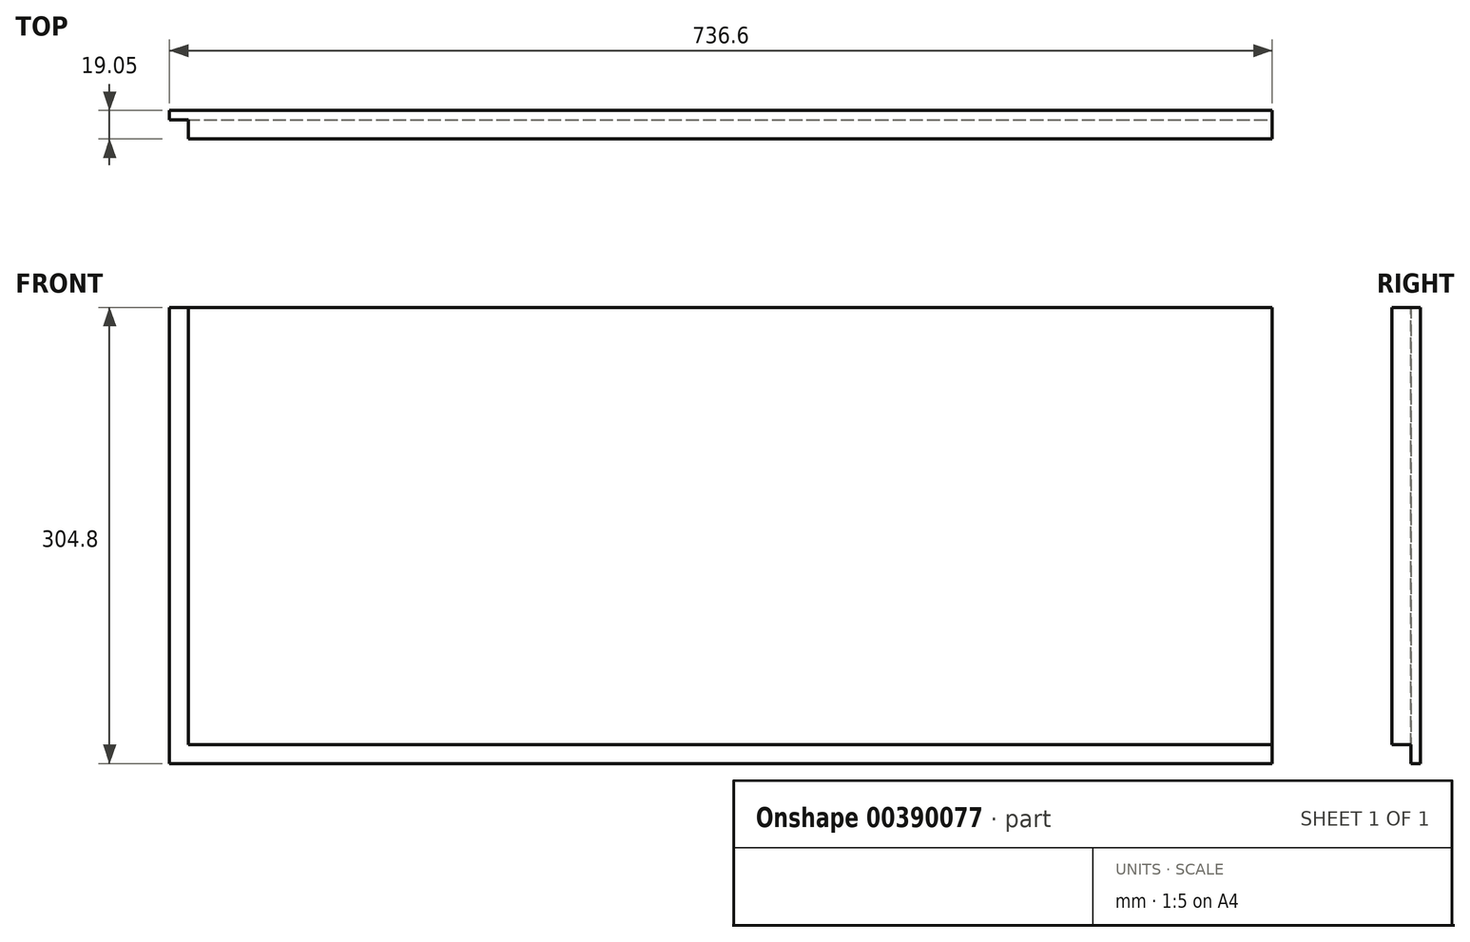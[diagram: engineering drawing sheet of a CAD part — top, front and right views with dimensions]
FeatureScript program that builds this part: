
annotation { "Feature Type Name" : "Feature", "Feature Type Description" : "" }
export const myFeature = defineFeature(function(context is Context, id is Id, definition is map)
    precondition{}
    {
        {
            var Q0;
            Q0=qCreatedBy(makeId("Front.planeOp"),FACE);
            var sketch = newSketch(context, id + "F0", { "sketchPlane" : qUnion([Q0])});
            skLineSegment(sketch, "E0.bottom", {"start": v(0, 0) * mm, "end": v(736.6, 0) * mm});
            skLineSegment(sketch, "E0.top", {"start": v(0, 304.8) * mm, "end": v(736.6, 304.8) * mm});
            skLineSegment(sketch, "E0.left", {"start": v(0, 0) * mm, "end": v(0, 304.8) * mm});
            skLineSegment(sketch, "E0.right", {"start": v(736.6, 0) * mm, "end": v(736.6, 304.8) * mm});
            skSolve(sketch);
        }
        {
            var Q0;
            Q0 = qSketchRegion(id + "F0", true);
            var Q1;
            Q1=makeQuery(id+"F0.imprint","IMPRINT",FACE,{"disambiguationData":[TD([[makeQuery(id+"F0.imprint","IMPRINT",EDGE,{"derivedFrom":sQuery(id+"F0.wireOp",EDGE,"E0.bottom")}),1.0]])]});
            extrude(context, id + "F1", {"entities" : qUnion([Q0, Q1]), "depth" : 19.05 * mm});
        }
        {
            var Q0;
            Q0=makeQuery(id+"F1.opExtrude","SWEPT_FACE",FACE,{"disambiguationData":[OSD([sQuery(id+"F0.wireOp",EDGE,"E0.right")])]});
            var sketch = newSketch(context, id + "F2", { "sketchPlane" : qUnion([Q0])});
            skLineSegment(sketch, "E1.bottom", {"start": v(-19.05, 0) * mm, "end": v(-6.35, 0) * mm});
            skLineSegment(sketch, "E1.top", {"start": v(-19.05, 12.7) * mm, "end": v(-6.35, 12.7) * mm});
            skLineSegment(sketch, "E1.left", {"start": v(-19.05, 0) * mm, "end": v(-19.05, 12.7) * mm});
            skLineSegment(sketch, "E1.right", {"start": v(-6.35, 0) * mm, "end": v(-6.35, 12.7) * mm});
            skSolve(sketch);
        }
        {
            var Q0;
            Q0 = qSketchRegion(id + "F2", true);
            extrude(context, id + "F3", {"entities" : qUnion([Q0]), "operationType" : NewBodyOperationType.REMOVE, "endBound" : BoundingType.THROUGH_ALL, "oppositeDirection" : true, "depth" : 25.4 * mm});
        }
        {
            var Q0;
            Q0=makeQuery(id+"F1.opExtrude","SWEPT_FACE",FACE,{"disambiguationData":[OSD([sQuery(id+"F0.wireOp",EDGE,"E0.top")])]});
            var sketch = newSketch(context, id + "F4", { "sketchPlane" : qUnion([Q0])});
            skLineSegment(sketch, "E2.bottom", {"start": v(0, -19.05) * mm, "end": v(12.7, -19.05) * mm});
            skLineSegment(sketch, "E2.top", {"start": v(0, -6.35) * mm, "end": v(12.7, -6.35) * mm});
            skLineSegment(sketch, "E2.left", {"start": v(0, -19.05) * mm, "end": v(0, -6.35) * mm});
            skLineSegment(sketch, "E2.right", {"start": v(12.7, -19.05) * mm, "end": v(12.7, -6.35) * mm});
            skSolve(sketch);
        }
        {
            var Q0;
            Q0 = qSketchRegion(id + "F4", true);
            extrude(context, id + "F5", {"entities" : qUnion([Q0]), "operationType" : NewBodyOperationType.REMOVE, "endBound" : BoundingType.THROUGH_ALL, "oppositeDirection" : true, "depth" : 25.4 * mm});
        }
    });
